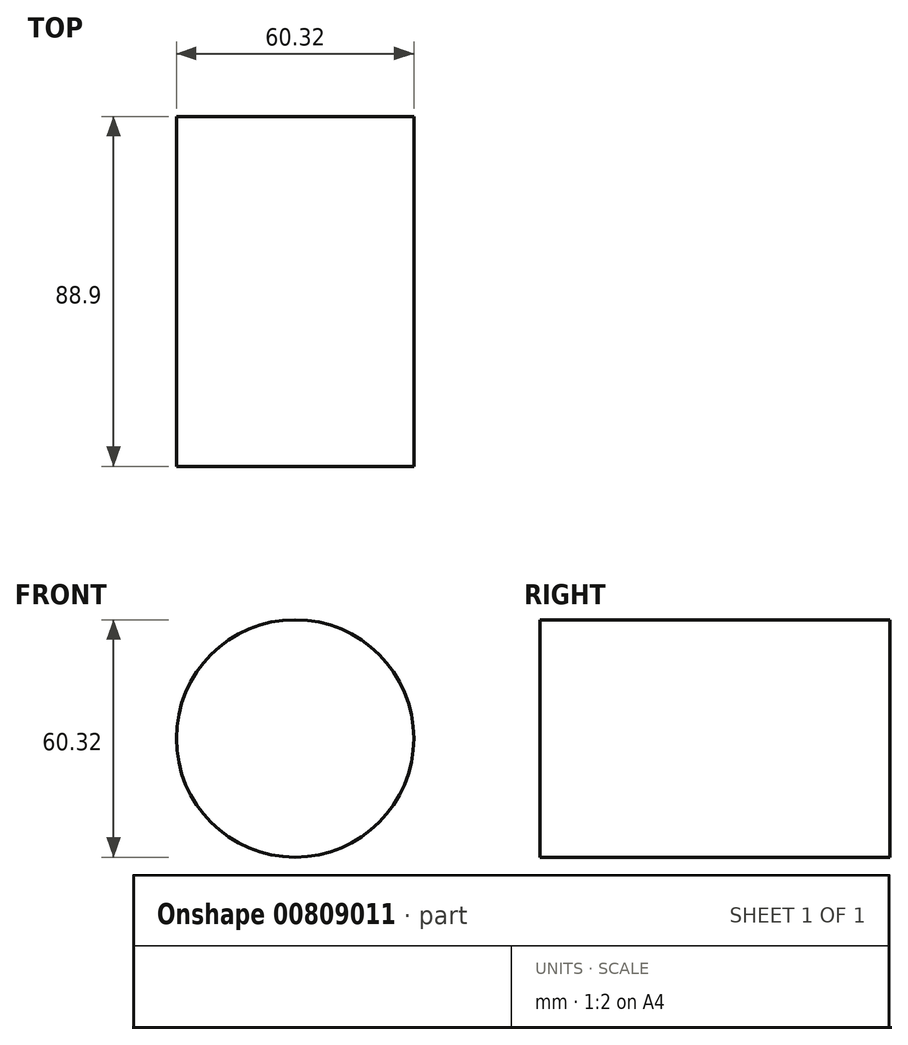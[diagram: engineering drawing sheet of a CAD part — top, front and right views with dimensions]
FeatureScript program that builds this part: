
annotation { "Feature Type Name" : "Feature", "Feature Type Description" : "" }
export const myFeature = defineFeature(function(context is Context, id is Id, definition is map)
    precondition{}
    {
        {
            var Q0;
            Q0=qCreatedBy(makeId("Front.planeOp"),FACE);
            var sketch = newSketch(context, id + "F0", { "sketchPlane" : qUnion([Q0])});
            skCircle(sketch, "E0", {"center": v(0, 0) * mm, "radius": 30.16 * mm});
            skSolve(sketch);
        }
        {
            var Q0;
            Q0=makeQuery(id+"F0.imprint","IMPRINT",FACE,{"disambiguationData":[TD([[makeQuery(id+"F0.imprint","IMPRINT",EDGE,{"derivedFrom":sQuery(id+"F0.wireOp",EDGE,"E0")}),1.0]])]});
            extrude(context, id + "F1", {"entities" : qUnion([Q0]), "depth" : 88.9 * mm, "offsetDistance" : 25.4 * mm});
        }
    });
